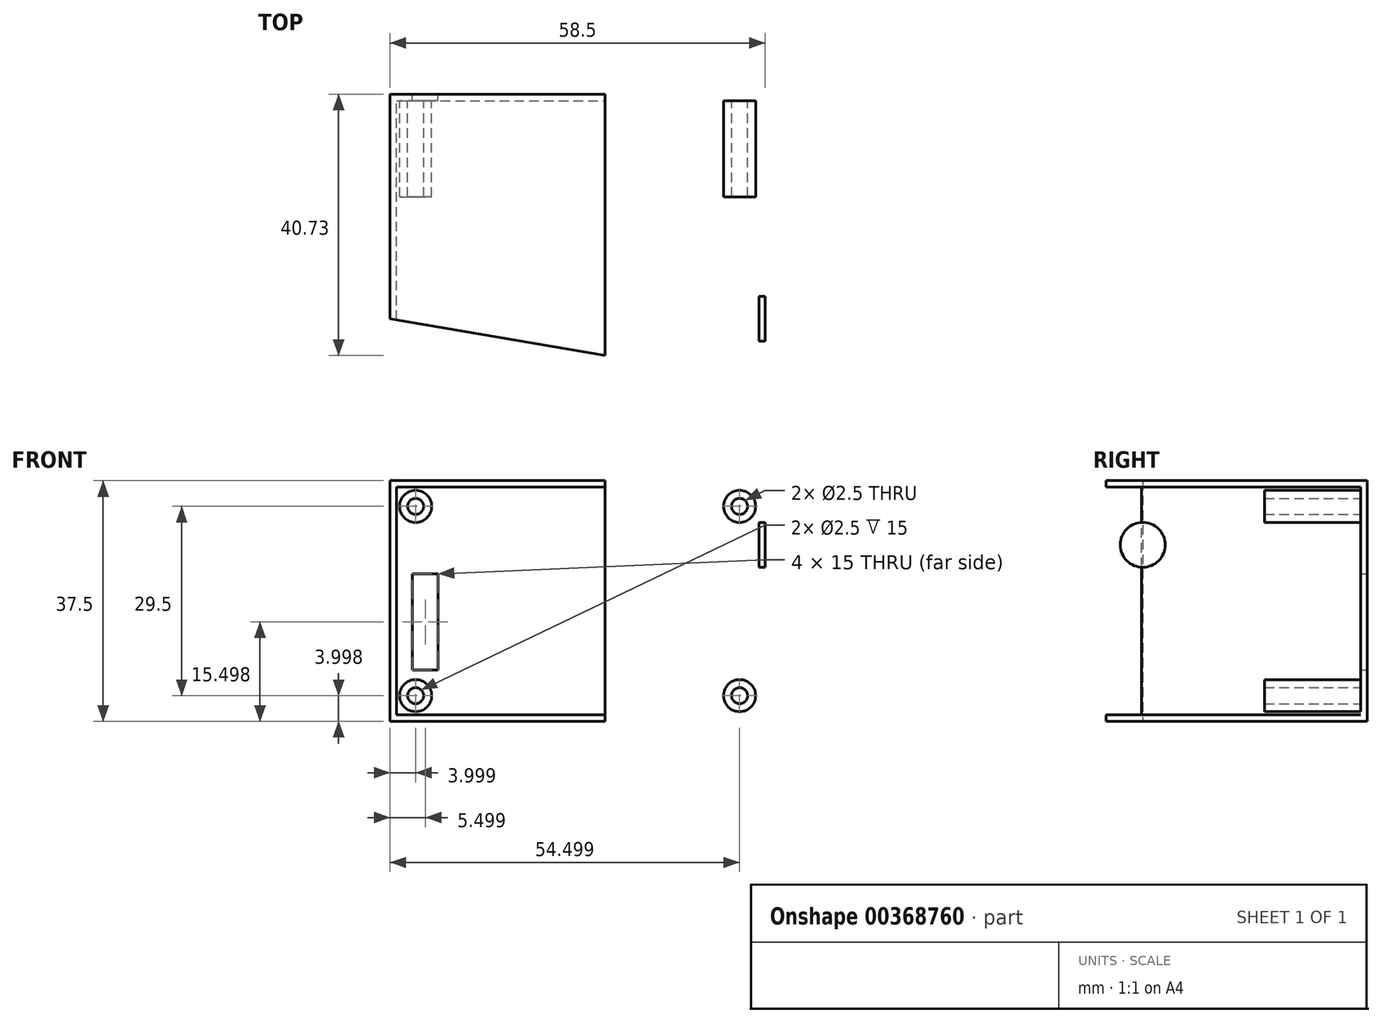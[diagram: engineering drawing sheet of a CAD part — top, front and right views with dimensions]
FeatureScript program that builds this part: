
annotation { "Feature Type Name" : "Feature", "Feature Type Description" : "" }
export const myFeature = defineFeature(function(context is Context, id is Id, definition is map)
    precondition{}
    {
        {
            var Q0;
            Q0=qCreatedBy(makeId("Front.planeOp"),FACE);
            var sketch = newSketch(context, id + "F0", { "sketchPlane" : qUnion([Q0])});
            skLineSegment(sketch, "E0.bottom", {"start": v(-164.68, -22.92) * mm, "end": v(-106.18, -22.92) * mm});
            skLineSegment(sketch, "E0.top", {"start": v(-164.68, -60.42) * mm, "end": v(-106.18, -60.42) * mm});
            skLineSegment(sketch, "E0.left", {"start": v(-164.68, -22.92) * mm, "end": v(-164.68, -60.42) * mm});
            skLineSegment(sketch, "E0.right", {"start": v(-106.18, -22.92) * mm, "end": v(-106.18, -60.42) * mm});
            skLineSegment(sketch, "E1.bottom", {"start": v(-161.18, -37.42) * mm, "end": v(-157.18, -37.42) * mm});
            skLineSegment(sketch, "E1.top", {"start": v(-161.18, -52.42) * mm, "end": v(-157.18, -52.42) * mm});
            skLineSegment(sketch, "E1.left", {"start": v(-161.18, -37.42) * mm, "end": v(-161.18, -52.42) * mm});
            skLineSegment(sketch, "E1.right", {"start": v(-157.18, -37.42) * mm, "end": v(-157.18, -52.42) * mm});
            skSolve(sketch);
        }
        {
            var Q0;
            Q0 = qSketchRegion(id + "F0", true);
            var Q1;
            Q1=makeQuery(id+"F0.imprint","IMPRINT",FACE,{"disambiguationData":[TD([[makeQuery(id+"F0.imprint","IMPRINT",EDGE,{"derivedFrom":sQuery(id+"F0.wireOp",EDGE,"E1.bottom")}),-1.0]])]});
            extrude(context, id + "F1", {"entities" : qUnion([Q0, Q1]), "depth" : 45 * mm, "offsetDistance" : 25 * mm});
        }
        {
            var Q0;
            Q0=makeQuery(id+"F1.opExtrude","CAP_FACE",FACE,{"disambiguationData":[OSD([sQuery(id+"F0.wireOp",EDGE,"E0.bottom"),sQuery(id+"F0.wireOp",EDGE,"E0.top"),sQuery(id+"F0.wireOp",EDGE,"E0.left"),sQuery(id+"F0.wireOp",EDGE,"E0.right"),sQuery(id+"F0.wireOp",EDGE,"E1.bottom"),sQuery(id+"F0.wireOp",EDGE,"E1.top"),sQuery(id+"F0.wireOp",EDGE,"E1.left"),sQuery(id+"F0.wireOp",EDGE,"E1.right")])],"isStart":false});
            shell(context, id + "F2", {"entities" : qUnion([Q0]), "thickness" : 1 * mm});
        }
        {
            var Q0;
            Q0=makeQuery(id+"F1.opExtrude","SWEPT_FACE",FACE,{"disambiguationData":[OSD([sQuery(id+"F0.wireOp",EDGE,"E0.top")])]});
            var sketch = newSketch(context, id + "F3", { "sketchPlane" : qUnion([Q0])});
            skLineSegment(sketch, "E2.bottom", {"start": v(-164.68, 35) * mm, "end": v(-106.18, 45) * mm});
            skLineSegment(sketch, "E2.top", {"start": v(-164.68, 0) * mm, "end": v(-106.18, 0) * mm});
            skLineSegment(sketch, "E2.left", {"start": v(-164.68, 35) * mm, "end": v(-164.68, 0) * mm});
            skLineSegment(sketch, "E2.right", {"start": v(-106.18, 45) * mm, "end": v(-106.18, 0) * mm});
            skLineSegment(sketch, "E3", {"start": v(-164.68, 35) * mm, "end": v(-164.68, 45) * mm});
            skLineSegment(sketch, "E4", {"start": v(-164.68, 45) * mm, "end": v(-106.18, 45) * mm});
            skSolve(sketch);
        }
        {
            var Q0;
            Q0=makeQuery(id+"F3.imprint","IMPRINT",FACE,{"disambiguationData":[TD([[makeQuery(id+"F3.imprint","IMPRINT",EDGE,{"derivedFrom":sQuery(id+"F3.wireOp",EDGE,"E2.bottom")}),1.0]])]});
            extrude(context, id + "F4", {"entities" : qUnion([Q0]), "operationType" : NewBodyOperationType.REMOVE, "oppositeDirection" : true, "depth" : 52.9 * mm, "offsetDistance" : 25 * mm});
        }
        {
            var Q0;
            Q0=makeQuery(id+"F1.opExtrude","SWEPT_FACE",FACE,{"disambiguationData":[OSD([sQuery(id+"F0.wireOp",EDGE,"E0.right")])]});
            var sketch = newSketch(context, id + "F5", { "sketchPlane" : qUnion([Q0])});
            skLineSegment(sketch, "E5.MirrorCS", {"start": v(0, -22.92) * mm, "end": v(-45, -22.92) * mm});
            skLineSegment(sketch, "E6.MirrorCS", {"start": v(-45, -22.92) * mm, "end": v(-45, -60.42) * mm});
            skLineSegment(sketch, "E7.MirrorCS", {"start": v(0, -22.92) * mm, "end": v(0, -60.42) * mm});
            skCircle(sketch, "E8.MirrorC", {"center": v(-35, -32.92) * mm, "radius": 3.5 * mm});
            skLineSegment(sketch, "E9.MirrorCS", {"start": v(0, -60.42) * mm, "end": v(-45, -60.42) * mm});
            skSolve(sketch);
        }
        {
            var Q0;
            Q0=makeQuery(id+"F5.imprint","IMPRINT",FACE,{"disambiguationData":[TD([[makeQuery(id+"F5.imprint","IMPRINT",EDGE,{"derivedFrom":sQuery(id+"F5.wireOp",EDGE,"0107eb3e-5638-4bb7-819e-3cb07afdfc9f")}),1.0]])]});
            var Q1;
            Q1=makeQuery(id+"F5.imprint","IMPRINT",FACE,{"disambiguationData":[TD([[makeQuery(id+"F5.imprint","IMPRINT",EDGE,{"derivedFrom":sQuery(id+"F5.wireOp",EDGE,"E8.MirrorC")}),-1.0]])]});
            extrude(context, id + "F6", {"entities" : qUnion([Q0, Q1]), "operationType" : NewBodyOperationType.REMOVE, "oppositeDirection" : true, "depth" : 25 * mm, "offsetDistance" : 25 * mm});
        }
        {
            var Q0;
            Q0=makeQuery(id+"F0.imprint","IMPRINT",FACE,{"disambiguationData":[TD([[makeQuery(id+"F0.imprint","IMPRINT",EDGE,{"derivedFrom":sQuery(id+"F0.wireOp",EDGE,"E1.bottom")}),-1.0]])]});
            extrude(context, id + "F7", {"entities" : qUnion([Q0]), "operationType" : NewBodyOperationType.REMOVE, "depth" : 25 * mm, "offsetDistance" : 25 * mm});
        }
        {
            var Q0;
            Q0=makeQuery(id+"F2.opShell","OFFSET_FACE",FACE,{"disambiguationData":[OSD([sQuery(id+"F0.wireOp",EDGE,"E0.bottom"),sQuery(id+"F0.wireOp",EDGE,"E0.top"),sQuery(id+"F0.wireOp",EDGE,"E0.left"),sQuery(id+"F0.wireOp",EDGE,"E0.right")])]});
            var sketch = newSketch(context, id + "F8", { "sketchPlane" : qUnion([Q0])});
            skCircle(sketch, "E10", {"center": v(-110.18, -26.92) * mm, "radius": 1.25 * mm});
            skCircle(sketch, "E11", {"center": v(-110.18, -26.92) * mm, "radius": 2.5 * mm});
            skCircle(sketch, "E12", {"center": v(-110.18, -56.42) * mm, "radius": 1.25 * mm});
            skCircle(sketch, "E13", {"center": v(-110.18, -56.42) * mm, "radius": 2.5 * mm});
            skCircle(sketch, "E14", {"center": v(-160.68, -56.42) * mm, "radius": 1.25 * mm});
            skCircle(sketch, "E15", {"center": v(-160.68, -56.42) * mm, "radius": 2.5 * mm});
            skCircle(sketch, "E16", {"center": v(-160.68, -26.92) * mm, "radius": 1.25 * mm});
            skCircle(sketch, "E17", {"center": v(-160.68, -26.92) * mm, "radius": 2.5 * mm});
            skSolve(sketch);
        }
        {
            var Q0;
            Q0 = qSketchRegion(id + "F8", true);
            extrude(context, id + "F9", {"entities" : qUnion([Q0]), "operationType" : NewBodyOperationType.ADD, "depth" : 15 * mm, "offsetDistance" : 25 * mm});
        }
    });
